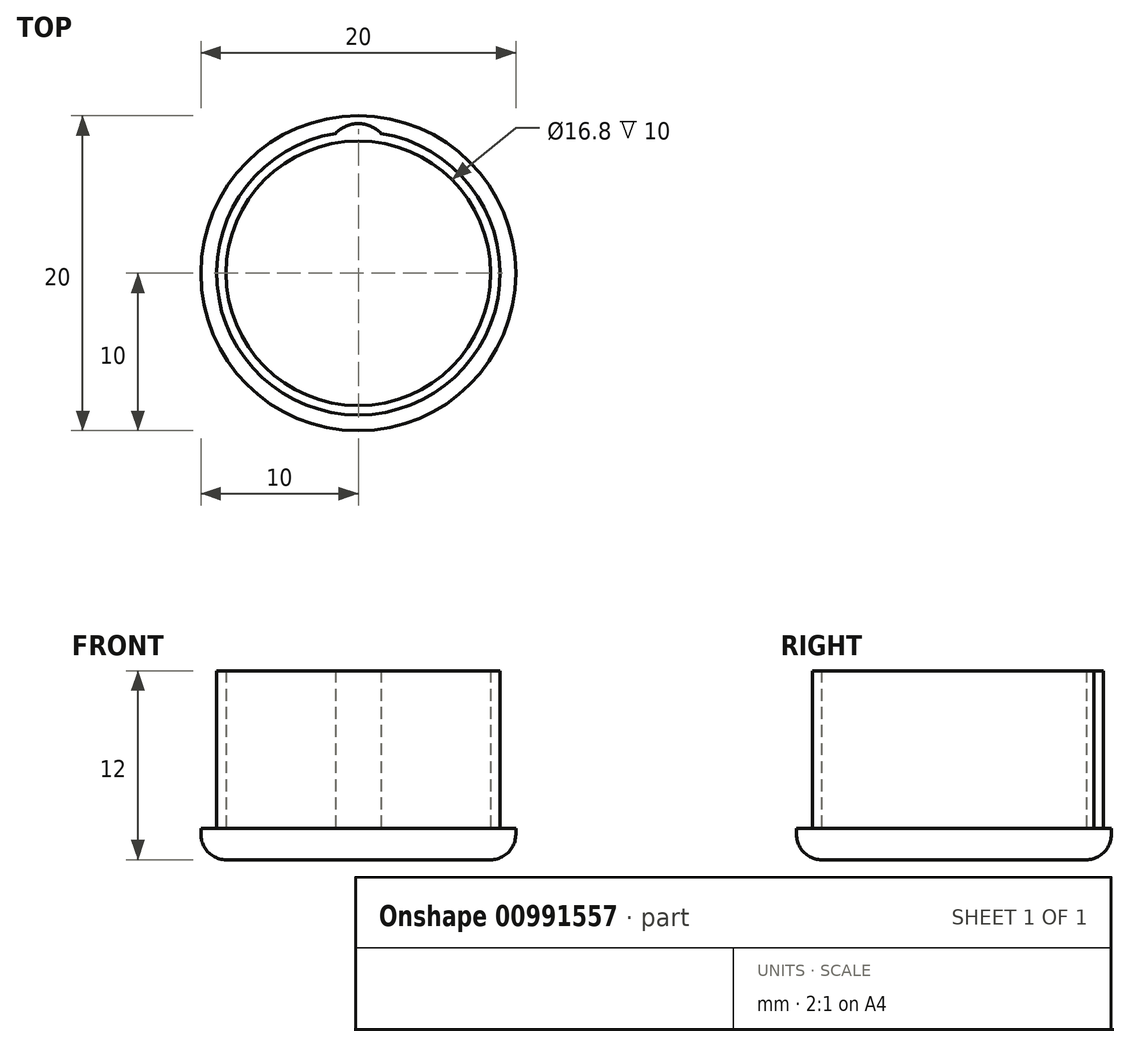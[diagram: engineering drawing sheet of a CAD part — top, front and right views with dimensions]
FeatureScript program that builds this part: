
annotation { "Feature Type Name" : "Feature", "Feature Type Description" : "" }
export const myFeature = defineFeature(function(context is Context, id is Id, definition is map)
    precondition{}
    {
        {
            var Q0;
            Q0=qCreatedBy(makeId("Top.planeOp"),FACE);
            var sketch = newSketch(context, id + "F0", { "sketchPlane" : qUnion([Q0])});
            skCircle(sketch, "E0", {"center": v(0, 0) * mm, "radius": 10 * mm});
            skSolve(sketch);
        }
        {
            var Q0;
            Q0=makeQuery(id+"F0.imprint","IMPRINT",FACE,{"disambiguationData":[TD([[makeQuery(id+"F0.imprint","IMPRINT",EDGE,{"derivedFrom":sQuery(id+"F0.wireOp",EDGE,"E0")}),1.0]])]});
            extrude(context, id + "F1", {"entities" : qUnion([Q0]), "depth" : 2 * mm, "offsetDistance" : 25 * mm});
        }
        {
            var Q0;
            Q0=makeQuery(id+"F1.opExtrude","CAP_EDGE",EDGE,{"disambiguationData":[OSD([sQuery(id+"F0.wireOp",EDGE,"E0")])],"isStart":true});
            fillet(context, id + "F2", {"entities" : qUnion([Q0]), "radius" : 1.6 * mm, "tangentPropagation" : true, "allowEdgeOverflow" : false});
        }
        {
            var Q0;
            Q0=makeQuery(id+"F1.opExtrude","CAP_FACE",FACE,{"disambiguationData":[OSD([sQuery(id+"F0.wireOp",EDGE,"E0")])],"isStart":false});
            var sketch = newSketch(context, id + "F3", { "sketchPlane" : qUnion([Q0])});
            skCircle(sketch, "E1", {"center": v(0, 0) * mm, "radius": 9 * mm});
            skCircle(sketch, "E2", {"center": v(0, 0) * mm, "radius": 8.4 * mm});
            skSolve(sketch);
        }
        {
            var Q0;
            Q0=makeQuery(id+"F3.imprint","IMPRINT",FACE,{"disambiguationData":[TD([[makeQuery(id+"F3.imprint","IMPRINT",EDGE,{"derivedFrom":sQuery(id+"F3.wireOp",EDGE,"E1")}),1.0]])]});
            var sketch = newSketch(context, id + "F4", { "sketchPlane" : qUnion([Q0])});
            skSolve(sketch);
        }
        {
            var Q0;
            Q0=makeQuery(id+"F4.imprint","IMPRINT",FACE,{"disambiguationData":[TD([[makeQuery(id+"F4.imprint","IMPRINT",EDGE,{"derivedFrom":makeQuery(id+"F3.imprint","IMPRINT",EDGE,{"derivedFrom":sQuery(id+"F3.wireOp",EDGE,"E1")})}),1.0]])]});
            extrude(context, id + "F5", {"entities" : qUnion([Q0]), "operationType" : NewBodyOperationType.ADD, "depth" : 10 * mm, "offsetDistance" : 25 * mm});
        }
        {
            var Q0;
            Q0=makeQuery(id+"F3.imprint","IMPRINT",FACE,{"disambiguationData":[TD([[makeQuery(id+"F3.imprint","IMPRINT",EDGE,{"derivedFrom":sQuery(id+"F3.wireOp",EDGE,"E1")}),-1.0]])]});
            var sketch = newSketch(context, id + "F6", { "sketchPlane" : qUnion([Q0])});
            skCircle(sketch, "E3.0", {"center": v(0, 0) * mm, "radius": 9 * mm});
            skArc(sketch, "E4", {"start": v(1.44, 8.88) * mm, "mid": v(0, 9.5) * mm, "end": v(-1.44, 8.88) * mm});
            skSolve(sketch);
        }
        {
            var Q0;
            {var subQ0=sQuery(id+"F6.wireOp",EDGE,"E4");Q0=makeQuery(id+"F6.imprint","IMPRINT",FACE,{"disambiguationData":[TD([[makeQuery(id+"F6.imprint","IMPRINT",EDGE,{"derivedFrom":subQ0}),1.0]])]});}
            var Q1;
            Q1=makeQuery(id+"F5.opExtrude","CAP_FACE",FACE,{"disambiguationData":[OSD([sQuery(id+"F3.wireOp",EDGE,"E1"),sQuery(id+"F3.wireOp",EDGE,"E2")])],"isStart":false});
            extrude(context, id + "F7", {"entities" : qUnion([Q0]), "operationType" : NewBodyOperationType.ADD, "endBound" : BoundingType.UP_TO_SURFACE, "depth" : 25 * mm, "endBoundEntityFace" : qUnion([Q1]), "offsetDistance" : 25 * mm});
        }
    });
